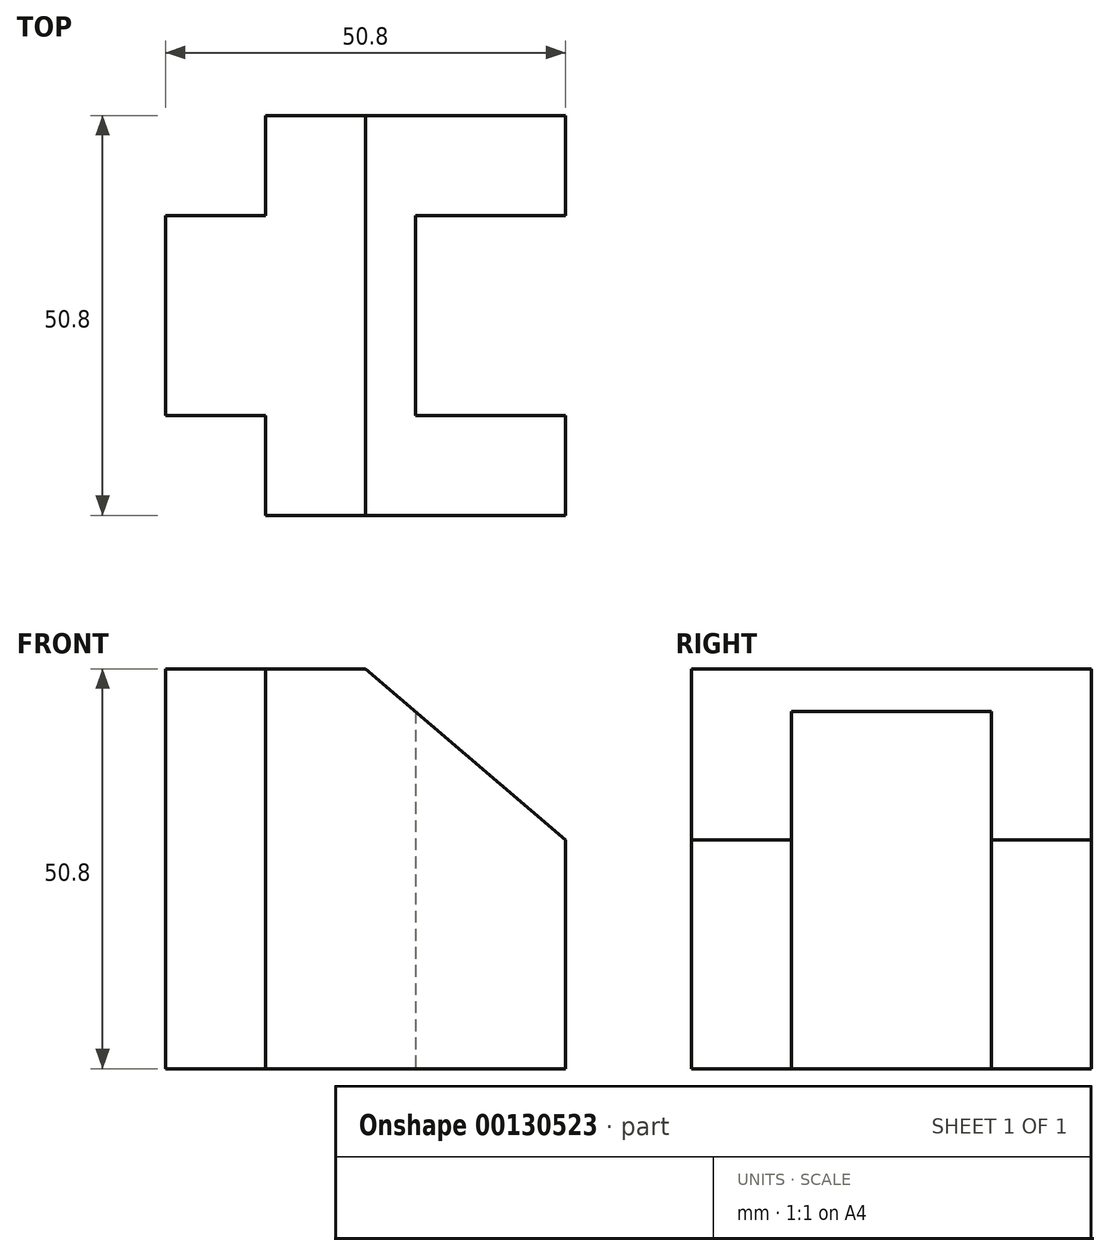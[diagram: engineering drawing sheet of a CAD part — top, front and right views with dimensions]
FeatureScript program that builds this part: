
annotation { "Feature Type Name" : "Feature", "Feature Type Description" : "" }
export const myFeature = defineFeature(function(context is Context, id is Id, definition is map)
    precondition{}
    {
        {
            var Q0;
            Q0=qCreatedBy(makeId("Front.planeOp"),FACE);
            var sketch = newSketch(context, id + "F0", { "sketchPlane" : qUnion([Q0])});
            skLineSegment(sketch, "E0", {"start": v(0, 0) * mm, "end": v(0, 50.8) * mm});
            skLineSegment(sketch, "E1", {"start": v(0, 50.8) * mm, "end": v(12.7, 50.8) * mm});
            skLineSegment(sketch, "E2", {"start": v(12.7, 50.8) * mm, "end": v(12.7, 0) * mm});
            skLineSegment(sketch, "E3", {"start": v(12.7, 0) * mm, "end": v(0, 0) * mm});
            skLineSegment(sketch, "E4", {"start": v(12.7, 50.8) * mm, "end": v(38.1, 29.03) * mm});
            skLineSegment(sketch, "E5", {"start": v(38.1, 29.03) * mm, "end": v(38.1, 0) * mm});
            skLineSegment(sketch, "E6", {"start": v(38.1, 0) * mm, "end": v(12.7, 0) * mm});
            skLineSegment(sketch, "E7", {"start": v(0, 0) * mm, "end": v(-12.7, 0) * mm});
            skLineSegment(sketch, "E8", {"start": v(-12.7, 0) * mm, "end": v(-12.7, 50.8) * mm});
            skLineSegment(sketch, "E9", {"start": v(-12.7, 50.8) * mm, "end": v(0, 50.8) * mm});
            skSolve(sketch);
        }
        {
            var Q0;
            Q0=makeQuery(id+"F0.imprint","IMPRINT",FACE,{"disambiguationData":[TD([[makeQuery(id+"F0.imprint","IMPRINT",EDGE,{"derivedFrom":sQuery(id+"F0.wireOp",EDGE,"E0")}),-1.0]])]});
            var Q1;
            Q1=makeQuery(id+"F0.imprint","IMPRINT",FACE,{"disambiguationData":[TD([[makeQuery(id+"F0.imprint","IMPRINT",EDGE,{"derivedFrom":sQuery(id+"F0.wireOp",EDGE,"E2")}),1.0]])]});
            extrude(context, id + "F1", {"entities" : qUnion([Q0, Q1]), "endBound" : BoundingType.SYMMETRIC, "depth" : 50.8 * mm});
        }
        {
            var Q0;
            Q0=makeQuery(id+"F0.imprint","IMPRINT",FACE,{"disambiguationData":[TD([[makeQuery(id+"F0.imprint","IMPRINT",EDGE,{"derivedFrom":sQuery(id+"F0.wireOp",EDGE,"E0")}),1.0]])]});
            extrude(context, id + "F2", {"entities" : qUnion([Q0]), "operationType" : NewBodyOperationType.ADD, "endBound" : BoundingType.SYMMETRIC, "depth" : 25.4 * mm});
        }
        {
            var Q0;
            Q0=qCreatedBy(makeId("Top.planeOp"),FACE);
            var sketch = newSketch(context, id + "F3", { "sketchPlane" : qUnion([Q0])});
            skLineSegment(sketch, "E10", {"start": v(19.05, -12.7) * mm, "end": v(19.05, 12.7) * mm});
            skLineSegment(sketch, "E11", {"start": v(19.05, 12.7) * mm, "end": v(38.1, 12.7) * mm});
            skLineSegment(sketch, "E12", {"start": v(38.1, 12.7) * mm, "end": v(38.1, -12.7) * mm});
            skLineSegment(sketch, "E13", {"start": v(38.1, -12.7) * mm, "end": v(19.05, -12.7) * mm});
            skSolve(sketch);
        }
        {
            var Q0;
            Q0 = qSketchRegion(id + "F3", true);
            extrude(context, id + "F4", {"entities" : qUnion([Q0]), "operationType" : NewBodyOperationType.REMOVE, "depth" : 50.8 * mm});
        }
    });
